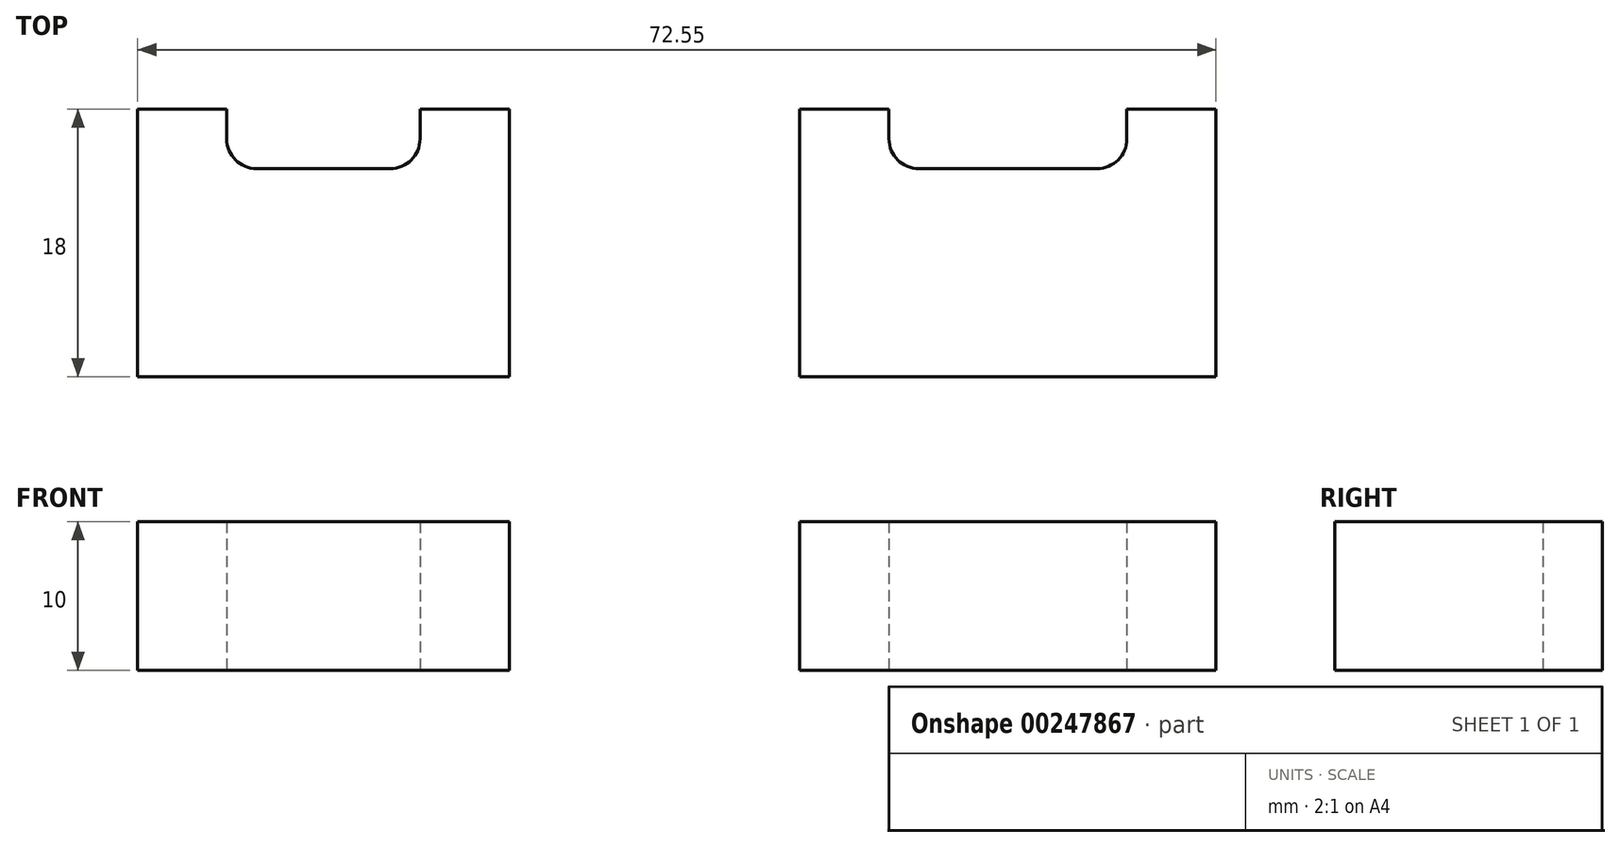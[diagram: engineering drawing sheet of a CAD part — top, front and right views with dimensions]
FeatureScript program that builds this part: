
annotation { "Feature Type Name" : "Feature", "Feature Type Description" : "" }
export const myFeature = defineFeature(function(context is Context, id is Id, definition is map)
    precondition{}
    {
        {
            var Q0;
            Q0=qCreatedBy(makeId("Top.planeOp"),FACE);
            var sketch = newSketch(context, id + "F0", { "sketchPlane" : qUnion([Q0])});
            skLineSegment(sketch, "E0.bottom", {"start": v(0, 18) * mm, "end": v(25, 18) * mm});
            skLineSegment(sketch, "E0.top", {"start": v(0, 0) * mm, "end": v(25, 0) * mm});
            skLineSegment(sketch, "E0.left", {"start": v(0, 18) * mm, "end": v(0, 0) * mm});
            skLineSegment(sketch, "E0.right", {"start": v(25, 18) * mm, "end": v(25, 0) * mm});
            skPoint(sketch, "E1", {"position": v(12.5, 18) * mm});
            skSolve(sketch);
        }
        {
            var Q0;
            Q0 = qSketchRegion(id + "F0", true);
            extrude(context, id + "F1", {"entities" : qUnion([Q0]), "depth" : 10 * mm});
        }
        {
            var Q0;
            Q0=qCreatedBy(makeId("Top.planeOp"),FACE);
            var sketch = newSketch(context, id + "F2", { "sketchPlane" : qUnion([Q0])});
            skLineSegment(sketch, "E2.bottom", {"start": v(6, 14) * mm, "end": v(19, 14) * mm});
            skLineSegment(sketch, "E2.top", {"start": v(6, 18) * mm, "end": v(19, 18) * mm});
            skLineSegment(sketch, "E2.left", {"start": v(6, 14) * mm, "end": v(6, 18) * mm});
            skLineSegment(sketch, "E2.right", {"start": v(19, 14) * mm, "end": v(19, 18) * mm});
            skPoint(sketch, "E3", {"position": v(12.5, 18) * mm});
            skSolve(sketch);
        }
        {
            var Q0;
            Q0 = qSketchRegion(id + "F2", true);
            extrude(context, id + "F3", {"entities" : qUnion([Q0]), "operationType" : NewBodyOperationType.REMOVE, "endBound" : BoundingType.THROUGH_ALL, "depth" : 25 * mm});
        }
        {
            var Q0;
            Q0=qCreatedBy(makeId("Top.planeOp"),FACE);
            var sketch = newSketch(context, id + "F4", { "sketchPlane" : qUnion([Q0])});
            skLineSegment(sketch, "E4.bottom", {"start": v(44.55, 18) * mm, "end": v(72.55, 18) * mm});
            skLineSegment(sketch, "E4.top", {"start": v(44.55, 0) * mm, "end": v(72.55, 0) * mm});
            skLineSegment(sketch, "E4.left", {"start": v(44.55, 18) * mm, "end": v(44.55, 0) * mm});
            skLineSegment(sketch, "E4.right", {"start": v(72.55, 18) * mm, "end": v(72.55, 0) * mm});
            skPoint(sketch, "E5", {"position": v(58.55, 18) * mm});
            skSolve(sketch);
        }
        {
            var Q0;
            Q0 = qSketchRegion(id + "F4", true);
            extrude(context, id + "F5", {"entities" : qUnion([Q0]), "depth" : 10 * mm});
        }
        {
            var Q0;
            Q0=qCreatedBy(makeId("Top.planeOp"),FACE);
            var sketch = newSketch(context, id + "F6", { "sketchPlane" : qUnion([Q0])});
            skLineSegment(sketch, "E6.bottom", {"start": v(50.55, 14) * mm, "end": v(66.55, 14) * mm});
            skLineSegment(sketch, "E6.top", {"start": v(50.55, 18) * mm, "end": v(66.55, 18) * mm});
            skLineSegment(sketch, "E6.left", {"start": v(50.55, 14) * mm, "end": v(50.55, 18) * mm});
            skLineSegment(sketch, "E6.right", {"start": v(66.55, 14) * mm, "end": v(66.55, 18) * mm});
            skPoint(sketch, "E7", {"position": v(58.55, 18) * mm});
            skSolve(sketch);
        }
        {
            var Q0;
            Q0 = qSketchRegion(id + "F6", true);
            extrude(context, id + "F7", {"entities" : qUnion([Q0]), "operationType" : NewBodyOperationType.REMOVE, "endBound" : BoundingType.THROUGH_ALL, "depth" : 25 * mm});
        }
        {
            var Q0;
            Q0=makeQuery(id+"F3.boolean.opBoolean","COPY",EDGE,{"derivedFrom":makeQuery(id+"F3.opExtrude","SWEPT_EDGE",EDGE,{"disambiguationData":[OSD([sQuery(id+"F2.wireOp",EDGE,"E2.bottom"),sQuery(id+"F2.wireOp",EDGE,"E2.left")])]})});
            var Q1;
            Q1=makeQuery(id+"F3.boolean.opBoolean","COPY",EDGE,{"derivedFrom":makeQuery(id+"F3.opExtrude","SWEPT_EDGE",EDGE,{"disambiguationData":[OSD([sQuery(id+"F2.wireOp",EDGE,"E2.bottom"),sQuery(id+"F2.wireOp",EDGE,"E2.right")])]})});
            var Q2;
            Q2=makeQuery(id+"F3.boolean.opBoolean","COPY",EDGE,{"derivedFrom":makeQuery(id+"F3.opExtrude","SWEPT_EDGE",EDGE,{"disambiguationData":[OSD([sQuery(id+"F2.wireOp",EDGE,"E2.top"),sQuery(id+"F2.wireOp",EDGE,"E2.left")])]})});
            var Q3;
            Q3=makeQuery(id+"F3.boolean.opBoolean","COPY",EDGE,{"derivedFrom":makeQuery(id+"F3.opExtrude","SWEPT_EDGE",EDGE,{"disambiguationData":[OSD([sQuery(id+"F2.wireOp",EDGE,"E2.top"),sQuery(id+"F2.wireOp",EDGE,"E2.right")])]})});
            var Q4;
            Q4=makeQuery(id+"F7.boolean.opBoolean","COPY",EDGE,{"derivedFrom":makeQuery(id+"F7.opExtrude","SWEPT_EDGE",EDGE,{"disambiguationData":[OSD([sQuery(id+"F6.wireOp",EDGE,"E6.top"),sQuery(id+"F6.wireOp",EDGE,"E6.left")])]})});
            var Q5;
            Q5=makeQuery(id+"F7.boolean.opBoolean","COPY",EDGE,{"derivedFrom":makeQuery(id+"F7.opExtrude","SWEPT_EDGE",EDGE,{"disambiguationData":[OSD([sQuery(id+"F6.wireOp",EDGE,"E6.bottom"),sQuery(id+"F6.wireOp",EDGE,"E6.left")])]})});
            var Q6;
            Q6=makeQuery(id+"F7.boolean.opBoolean","COPY",EDGE,{"derivedFrom":makeQuery(id+"F7.opExtrude","SWEPT_EDGE",EDGE,{"disambiguationData":[OSD([sQuery(id+"F6.wireOp",EDGE,"E6.bottom"),sQuery(id+"F6.wireOp",EDGE,"E6.right")])]})});
            var Q7;
            Q7=makeQuery(id+"F7.boolean.opBoolean","COPY",EDGE,{"derivedFrom":makeQuery(id+"F7.opExtrude","SWEPT_EDGE",EDGE,{"disambiguationData":[OSD([sQuery(id+"F6.wireOp",EDGE,"E6.top"),sQuery(id+"F6.wireOp",EDGE,"E6.right")])]})});
            fillet(context, id + "F8", {"entities" : qUnion([Q0, Q1, Q2, Q3, Q4, Q5, Q6, Q7]), "radius" : 2 * mm, "tangentPropagation" : true, "allowEdgeOverflow" : false});
        }
    });
